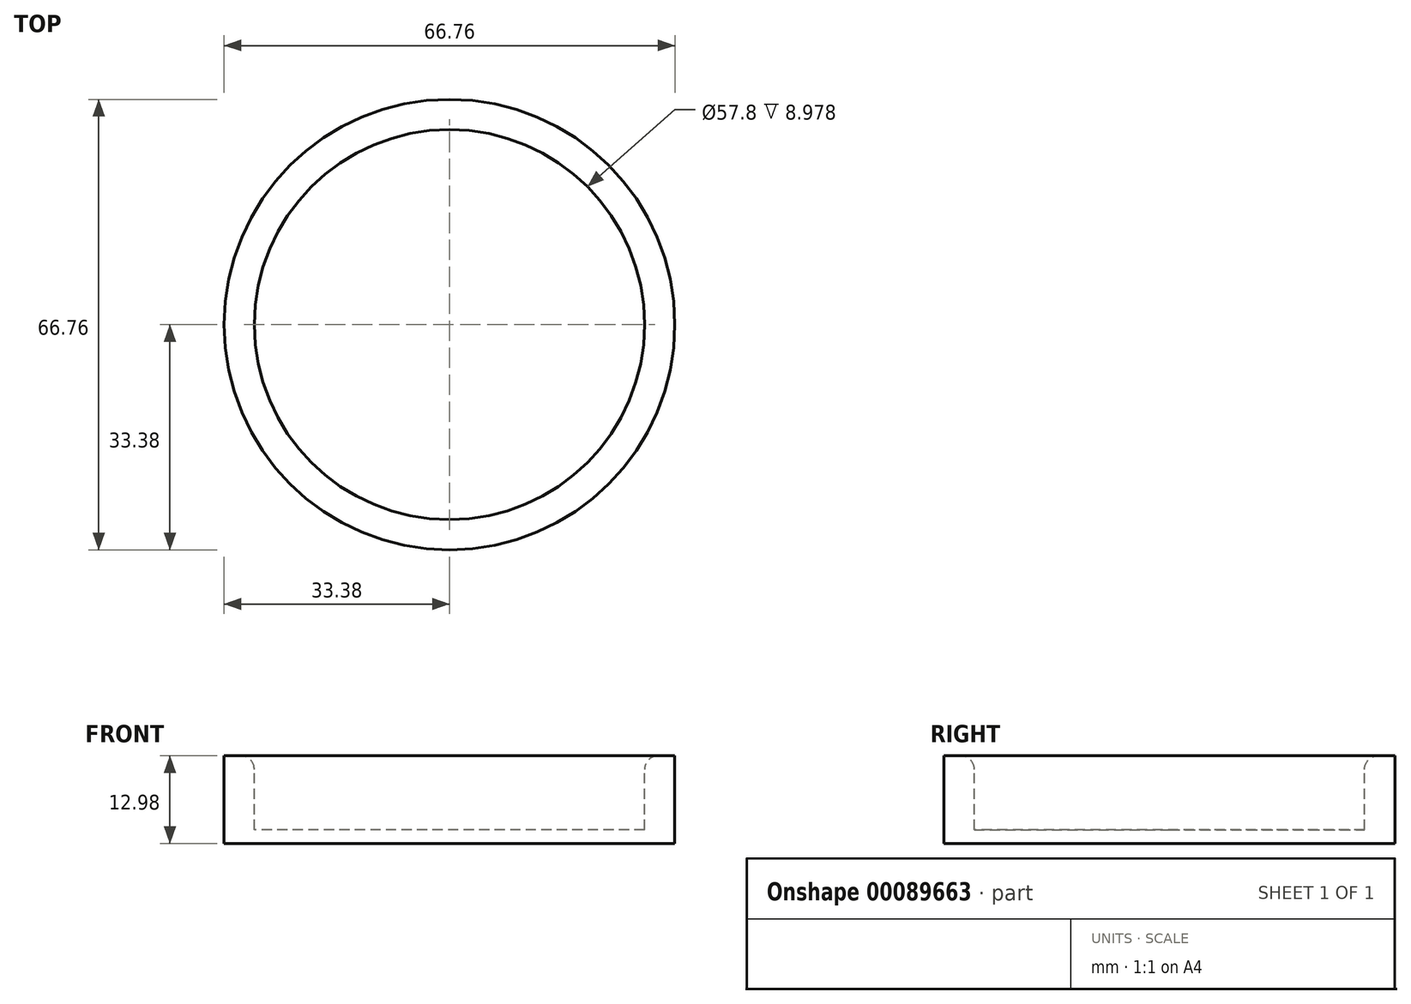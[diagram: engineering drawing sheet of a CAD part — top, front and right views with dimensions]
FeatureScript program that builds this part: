
annotation { "Feature Type Name" : "Feature", "Feature Type Description" : "" }
export const myFeature = defineFeature(function(context is Context, id is Id, definition is map)
    precondition{}
    {
        {
            var Q0;
            Q0=qCreatedBy(makeId("Front.planeOp"),FACE);
            var sketch = newSketch(context, id + "F0", { "sketchPlane" : qUnion([Q0])});
            skLineSegment(sketch, "E0", {"start": v(-33.38, 0) * mm, "end": v(0, 0) * mm});
            skLineSegment(sketch, "E1", {"start": v(0, 0) * mm, "end": v(0, 2) * mm});
            skLineSegment(sketch, "E2", {"start": v(0, 2) * mm, "end": v(-28.9, 2) * mm});
            skLineSegment(sketch, "E3", {"start": v(-28.9, 2) * mm, "end": v(-28.9, 10.98) * mm});
            skLineSegment(sketch, "E4", {"start": v(-30.9, 12.98) * mm, "end": v(-33.38, 12.98) * mm});
            skLineSegment(sketch, "E5", {"start": v(-33.38, 12.98) * mm, "end": v(-33.38, 0) * mm});
            skLineSegment(sketch, "E6", {"start": v(0, 25.52) * mm, "end": v(0, -14.44) * mm, "construction": true});
            skPoint(sketch, "E7.visualSharp", {"position": v(-28.9, 12.98) * mm});
            skArc(sketch, "E7.filletArc", {"start": v(-28.9, 10.98) * mm, "mid": v(-29.48, 12.4) * mm, "end": v(-30.9, 12.98) * mm});
            skSolve(sketch);
        }
        {
            var Q0;
            Q0=makeQuery(id+"F0.imprint","IMPRINT",FACE,{"disambiguationData":[TD([[makeQuery(id+"F0.imprint","IMPRINT",EDGE,{"derivedFrom":sQuery(id+"F0.wireOp",EDGE,"E0")}),1.0]])]});
            var Q1;
            Q1=sQuery(id+"F0.wireOp",EDGE,"E6");
            revolve(context, id + "F1", {"entities" : qUnion([Q0]), "axis" : qUnion([Q1]), "revolveType" : RevolveType.FULL});
        }
    });
